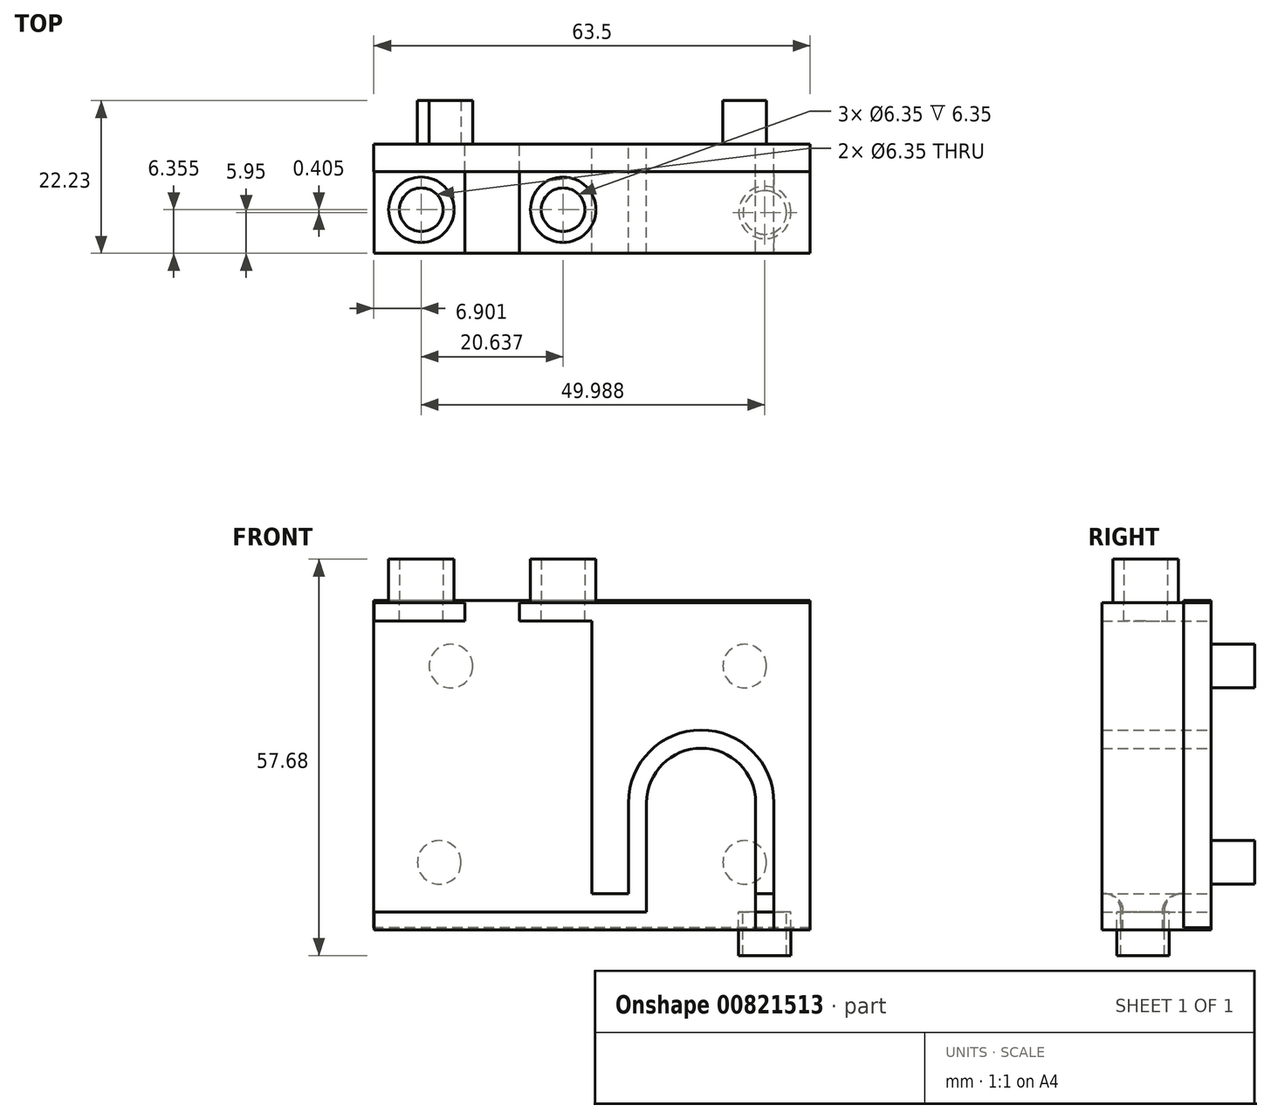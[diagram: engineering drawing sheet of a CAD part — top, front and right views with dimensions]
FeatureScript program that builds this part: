
annotation { "Feature Type Name" : "Feature", "Feature Type Description" : "" }
export const myFeature = defineFeature(function(context is Context, id is Id, definition is map)
    precondition{}
    {
        {
            var Q0;
            Q0=qCreatedBy(makeId("Front.planeOp"),FACE);
            var sketch = newSketch(context, id + "F0", { "sketchPlane" : qUnion([Q0])});
            skLineSegment(sketch, "E0.bottom", {"start": v(-31.75, 44.98) * mm, "end": v(0, 44.98) * mm});
            skLineSegment(sketch, "E0.top", {"start": v(-31.75, 0) * mm, "end": v(0, 0) * mm});
            skLineSegment(sketch, "E0.left", {"start": v(-31.75, 44.98) * mm, "end": v(-31.75, 0) * mm});
            skLineSegment(sketch, "E0.right", {"start": v(0, 44.98) * mm, "end": v(0, 0) * mm});
            skLineSegment(sketch, "E1.bottom", {"start": v(-26.46, 0) * mm, "end": v(-23.81, 0) * mm});
            skLineSegment(sketch, "E1.top", {"start": v(-26.46, 15.88) * mm, "end": v(-23.81, 15.88) * mm});
            skLineSegment(sketch, "E1.left", {"start": v(-26.46, 0) * mm, "end": v(-26.46, 15.87) * mm});
            skLineSegment(sketch, "E1.right", {"start": v(-23.81, 0) * mm, "end": v(-23.81, 15.87) * mm});
            skLineSegment(sketch, "E2.bottom", {"start": v(-7.94, 0) * mm, "end": v(-5.3, 0) * mm});
            skLineSegment(sketch, "E2.top", {"start": v(-7.94, 15.88) * mm, "end": v(-5.3, 15.88) * mm});
            skLineSegment(sketch, "E2.left", {"start": v(-7.94, 0) * mm, "end": v(-7.94, 15.87) * mm});
            skLineSegment(sketch, "E2.right", {"start": v(-5.3, 0) * mm, "end": v(-5.3, 15.87) * mm});
            skArc(sketch, "E3", {"start": v(-5.3, 15.87) * mm, "mid": v(-15.87, 26.46) * mm, "end": v(-26.46, 15.88) * mm});
            skArc(sketch, "E4", {"start": v(-7.94, 15.87) * mm, "mid": v(-15.87, 23.81) * mm, "end": v(-23.81, 15.87) * mm});
            skLineSegment(sketch, "E5.bottom", {"start": v(-26.46, 0) * mm, "end": v(-31.75, 0) * mm});
            skLineSegment(sketch, "E5.top", {"start": v(-26.46, 2.65) * mm, "end": v(-31.75, 2.65) * mm});
            skLineSegment(sketch, "E5.left", {"start": v(-26.46, 0) * mm, "end": v(-26.46, 2.65) * mm});
            skLineSegment(sketch, "E5.right", {"start": v(-31.75, 0) * mm, "end": v(-31.75, 2.65) * mm});
            skLineSegment(sketch, "E6.bottom", {"start": v(-31.75, 44.98) * mm, "end": v(-63.47, 44.98) * mm});
            skLineSegment(sketch, "E6.top", {"start": v(-31.75, 42.34) * mm, "end": v(-63.47, 42.34) * mm});
            skLineSegment(sketch, "E6.left", {"start": v(-31.75, 44.98) * mm, "end": v(-31.75, 42.34) * mm});
            skLineSegment(sketch, "E6.right", {"start": v(-63.47, 44.98) * mm, "end": v(-63.47, 42.34) * mm});
            skLineSegment(sketch, "E7.bottom", {"start": v(-63.47, 42.34) * mm, "end": v(-60.82, 42.34) * mm});
            skLineSegment(sketch, "E7.top", {"start": v(-63.47, 0) * mm, "end": v(-60.82, 0) * mm});
            skLineSegment(sketch, "E7.left", {"start": v(-63.47, 42.34) * mm, "end": v(-63.47, 0) * mm});
            skLineSegment(sketch, "E7.right", {"start": v(-60.82, 42.34) * mm, "end": v(-60.82, 0) * mm});
            skLineSegment(sketch, "E8.bottom", {"start": v(-63.47, 0) * mm, "end": v(0, 0) * mm});
            skLineSegment(sketch, "E8.top", {"start": v(-63.47, -2.65) * mm, "end": v(0, -2.65) * mm});
            skLineSegment(sketch, "E8.left", {"start": v(-63.47, 0) * mm, "end": v(-63.47, -2.65) * mm});
            skLineSegment(sketch, "E8.right", {"start": v(0, 0) * mm, "end": v(0, -2.65) * mm});
            skLineSegment(sketch, "E9.top", {"start": v(-7.94, -2.65) * mm, "end": v(-5.3, -2.65) * mm});
            skLineSegment(sketch, "E9.left", {"start": v(-7.94, 0) * mm, "end": v(-7.94, -2.65) * mm});
            skLineSegment(sketch, "E9.right", {"start": v(-5.3, 0) * mm, "end": v(-5.3, -2.65) * mm});
            skLineSegment(sketch, "E10.bottom", {"start": v(-58.18, 44.98) * mm, "end": v(-55.53, 44.98) * mm});
            skLineSegment(sketch, "E10.top", {"start": v(-58.18, 42.34) * mm, "end": v(-55.53, 42.34) * mm});
            skLineSegment(sketch, "E11.bottom", {"start": v(-50.25, 44.98) * mm, "end": v(-42.31, 44.98) * mm});
            skLineSegment(sketch, "E11.top", {"start": v(-50.25, 42.34) * mm, "end": v(-42.31, 42.34) * mm});
            skLineSegment(sketch, "E11.left", {"start": v(-50.25, 44.98) * mm, "end": v(-50.25, 42.34) * mm});
            skLineSegment(sketch, "E11.right", {"start": v(-42.31, 44.98) * mm, "end": v(-42.31, 42.34) * mm});
            skLineSegment(sketch, "E12.bottom", {"start": v(-37.04, 44.98) * mm, "end": v(-34.4, 44.98) * mm});
            skLineSegment(sketch, "E12.top", {"start": v(-37.04, 42.34) * mm, "end": v(-34.4, 42.34) * mm});
            skSolve(sketch);
        }
        {
            var Q0;
            Q0=makeQuery(id+"F0.imprint","IMPRINT",FACE,{"disambiguationData":[TD([[makeQuery(id+"F0.imprint","IMPRINT",EDGE,{"derivedFrom":sQuery(id+"F0.wireOp",EDGE,"E0.bottom")}),-1.0]])]});
            var Q1;
            {var subQ0=sQuery(id+"F0.wireOp",EDGE,"E1.right");Q1=makeQuery(id+"F0.imprint","IMPRINT",FACE,{"disambiguationData":[TD([[makeQuery(id+"F0.imprint","IMPRINT",EDGE,{"derivedFrom":subQ0}),-1.0]])]});}
            var Q2;
            {var subQ6=sQuery(id+"F0.wireOp",EDGE,"E8.left");Q2=makeQuery(id+"F0.imprint","IMPRINT",FACE,{"disambiguationData":[TD([[makeQuery(id+"F0.imprint","IMPRINT",EDGE,{"derivedFrom":subQ6}),1.0]])]});}
            var Q3;
            {var subQ0=sQuery(id+"F0.wireOp",EDGE,"E8.right");Q3=makeQuery(id+"F0.imprint","IMPRINT",FACE,{"disambiguationData":[TD([[makeQuery(id+"F0.imprint","IMPRINT",EDGE,{"derivedFrom":subQ0}),-1.0]])]});}
            var Q4;
            Q4=makeQuery(id+"F0.imprint","IMPRINT",FACE,{"disambiguationData":[TD([[makeQuery(id+"F0.imprint","IMPRINT",EDGE,{"derivedFrom":sQuery(id+"F0.wireOp",EDGE,"E7.bottom")}),-1.0]])]});
            var Q5;
            {var subQ1=sQuery(id+"F0.wireOp",EDGE,"E6.right");Q5=makeQuery(id+"F0.imprint","IMPRINT",FACE,{"disambiguationData":[TD([[makeQuery(id+"F0.imprint","IMPRINT",EDGE,{"derivedFrom":subQ1}),1.0]])]});}
            var Q6;
            {var subQ0=sQuery(id+"F0.wireOp",EDGE,"E10.right");Q6=makeQuery(id+"F0.imprint","IMPRINT",FACE,{"disambiguationData":[TD([[makeQuery(id+"F0.imprint","IMPRINT",EDGE,{"derivedFrom":subQ0}),1.0]])]});}
            var Q7;
            {var subQ0=sQuery(id+"F0.wireOp",EDGE,"E11.right");Q7=makeQuery(id+"F0.imprint","IMPRINT",FACE,{"disambiguationData":[TD([[makeQuery(id+"F0.imprint","IMPRINT",EDGE,{"derivedFrom":subQ0}),1.0]])]});}
            var Q8;
            {var subQ0=sQuery(id+"F0.wireOp",EDGE,"E6.left");Q8=makeQuery(id+"F0.imprint","IMPRINT",FACE,{"disambiguationData":[TD([[makeQuery(id+"F0.imprint","IMPRINT",EDGE,{"derivedFrom":subQ0}),-1.0]])]});}
            extrude(context, id + "F1", {"entities" : qUnion([Q0, Q1, Q2, Q3, Q4, Q5, Q6, Q7, Q8]), "depth" : 15.88 * mm, "offsetDistance" : 25.4 * mm});
        }
        {
            var Q0;
            Q0=qCreatedBy(makeId("Front.planeOp"),FACE);
            var sketch = newSketch(context, id + "F2", { "sketchPlane" : qUnion([Q0])});
            skLineSegment(sketch, "E13.bottom", {"start": v(0, 45.3) * mm, "end": v(-63.5, 45.3) * mm});
            skLineSegment(sketch, "E13.top", {"start": v(0, -2.33) * mm, "end": v(-63.5, -2.33) * mm});
            skLineSegment(sketch, "E13.left", {"start": v(0, 45.3) * mm, "end": v(0, -2.33) * mm});
            skLineSegment(sketch, "E13.right", {"start": v(-63.5, 45.3) * mm, "end": v(-63.5, -2.33) * mm});
            skCircle(sketch, "E14", {"center": v(-9.53, 35.77) * mm, "radius": 3.18 * mm});
            skCircle(sketch, "E15", {"center": v(-52.28, 35.77) * mm, "radius": 3.18 * mm});
            skCircle(sketch, "E16", {"center": v(-53.97, 7.2) * mm, "radius": 3.18 * mm});
            skCircle(sketch, "E17", {"center": v(-9.52, 7.2) * mm, "radius": 3.18 * mm});
            skSolve(sketch);
        }
        {
            var Q0;
            Q0 = qSketchRegion(id + "F2", true);
            var Q1;
            Q1=makeQuery(id+"F2.imprint","IMPRINT",FACE,{"disambiguationData":[TD([[makeQuery(id+"F2.imprint","IMPRINT",EDGE,{"derivedFrom":sQuery(id+"F2.wireOp",EDGE,"E15")}),1.0]])]});
            var Q2;
            Q2=makeQuery(id+"F2.imprint","IMPRINT",FACE,{"disambiguationData":[TD([[makeQuery(id+"F2.imprint","IMPRINT",EDGE,{"derivedFrom":sQuery(id+"F2.wireOp",EDGE,"E16")}),1.0]])]});
            var Q3;
            Q3=makeQuery(id+"F2.imprint","IMPRINT",FACE,{"disambiguationData":[TD([[makeQuery(id+"F2.imprint","IMPRINT",EDGE,{"derivedFrom":sQuery(id+"F2.wireOp",EDGE,"E17")}),1.0]])]});
            var Q4;
            Q4=makeQuery(id+"F2.imprint","IMPRINT",FACE,{"disambiguationData":[TD([[makeQuery(id+"F2.imprint","IMPRINT",EDGE,{"derivedFrom":sQuery(id+"F2.wireOp",EDGE,"E14")}),1.0]])]});
            extrude(context, id + "F3", {"entities" : qUnion([Q0, Q1, Q2, Q3, Q4]), "depth" : 3.97 * mm, "offsetDistance" : 25.4 * mm});
        }
        {
            var Q0;
            Q0=makeQuery(id+"F2.imprint","IMPRINT",FACE,{"disambiguationData":[TD([[makeQuery(id+"F2.imprint","IMPRINT",EDGE,{"derivedFrom":sQuery(id+"F2.wireOp",EDGE,"E14")}),1.0]])]});
            var Q1;
            Q1=makeQuery(id+"F2.imprint","IMPRINT",FACE,{"disambiguationData":[TD([[makeQuery(id+"F2.imprint","IMPRINT",EDGE,{"derivedFrom":sQuery(id+"F2.wireOp",EDGE,"E15")}),1.0]])]});
            var Q2;
            Q2=makeQuery(id+"F2.imprint","IMPRINT",FACE,{"disambiguationData":[TD([[makeQuery(id+"F2.imprint","IMPRINT",EDGE,{"derivedFrom":sQuery(id+"F2.wireOp",EDGE,"E17")}),1.0]])]});
            var Q3;
            Q3=makeQuery(id+"F2.imprint","IMPRINT",FACE,{"disambiguationData":[TD([[makeQuery(id+"F2.imprint","IMPRINT",EDGE,{"derivedFrom":sQuery(id+"F2.wireOp",EDGE,"E16")}),1.0]])]});
            var Q4;
            Q4=sQuery(id+"F2.wireOp",EDGE,"E14");
            var Q5;
            Q5=sQuery(id+"F2.wireOp",EDGE,"E15");
            var Q6;
            Q6=sQuery(id+"F2.wireOp",EDGE,"E17");
            var Q7;
            Q7=sQuery(id+"F2.wireOp",EDGE,"E16");
            extrude(context, id + "F4", {"entities" : qUnion([Q0, Q1, Q2, Q3]), "surfaceEntities" : qUnion([Q4, Q5, Q6, Q7]), "oppositeDirection" : true, "depth" : 6.35 * mm, "offsetDistance" : 25.4 * mm});
        }
        {
            var Q0;
            Q0=makeQuery(id+"F1.opExtrude","SWEPT_FACE",FACE,{"disambiguationData":[OSD([sQuery(id+"F0.wireOp",EDGE,"E6.bottom"),sQuery(id+"F0.wireOp",EDGE,"E10.bottom")])]});
            var sketch = newSketch(context, id + "F5", { "sketchPlane" : qUnion([Q0])});
            skCircle(sketch, "E18", {"center": v(-56.6, -9.52) * mm, "radius": 3.18 * mm});
            skCircle(sketch, "E19", {"center": v(-35.96, -9.52) * mm, "radius": 3.18 * mm});
            skCircle(sketch, "E20", {"center": v(-56.6, -9.52) * mm, "radius": 4.76 * mm});
            skCircle(sketch, "E21", {"center": v(-35.96, -9.52) * mm, "radius": 4.76 * mm});
            skSolve(sketch);
        }
        {
            var Q0;
            Q0 = qSketchRegion(id + "F5", true);
            extrude(context, id + "F6", {"entities" : qUnion([Q0]), "depth" : 6.35 * mm, "offsetDistance" : 25.4 * mm});
        }
        {
            var Q0;
            Q0=makeQuery(id+"F1.opExtrude","SWEPT_FACE",FACE,{"disambiguationData":[OSD([sQuery(id+"F0.wireOp",EDGE,"E6.bottom"),sQuery(id+"F0.wireOp",EDGE,"E10.bottom")])]});
            var sketch = newSketch(context, id + "F7", { "sketchPlane" : qUnion([Q0])});
            skCircle(sketch, "E22", {"center": v(-35.96, -9.52) * mm, "radius": 3.18 * mm});
            skCircle(sketch, "E23", {"center": v(-56.6, -9.52) * mm, "radius": 3.18 * mm});
            skSolve(sketch);
        }
        {
            var Q0;
            Q0 = qSketchRegion(id + "F7", true);
            extrude(context, id + "F8", {"entities" : qUnion([Q0]), "operationType" : NewBodyOperationType.REMOVE, "oppositeDirection" : true, "depth" : 25.4 * mm, "offsetDistance" : 25.4 * mm});
        }
        {
            var Q0;
            Q0=qCreatedBy(makeId("Top.planeOp"),FACE);
            var sketch = newSketch(context, id + "F9", { "sketchPlane" : qUnion([Q0])});
            skCircle(sketch, "E24", {"center": v(-6.61, -9.93) * mm, "radius": 3.81 * mm});
            skCircle(sketch, "E25", {"center": v(-6.61, -9.93) * mm, "radius": 3.18 * mm});
            skSolve(sketch);
        }
        {
            var Q0;
            Q0 = qSketchRegion(id + "F9", true);
            extrude(context, id + "F10", {"entities" : qUnion([Q0]), "oppositeDirection" : true, "depth" : 6.35 * mm, "offsetDistance" : 25.4 * mm});
        }
        {
            var Q0;
            Q0=qCreatedBy(makeId("Top.planeOp"),FACE);
            var sketch = newSketch(context, id + "F11", { "sketchPlane" : qUnion([Q0])});
            skLineSegment(sketch, "E26.bottom", {"start": v(-7.96, -15.88) * mm, "end": v(-5.31, -15.88) * mm});
            skLineSegment(sketch, "E26.top", {"start": v(-7.96, -3.95) * mm, "end": v(-5.31, -3.95) * mm});
            skLineSegment(sketch, "E26.left", {"start": v(-7.96, -15.88) * mm, "end": v(-7.96, -3.95) * mm});
            skLineSegment(sketch, "E26.right", {"start": v(-5.31, -15.88) * mm, "end": v(-5.31, -3.95) * mm});
            skCircle(sketch, "E27", {"center": v(-6.61, -9.93) * mm, "radius": 3.17 * mm});
            skSolve(sketch);
        }
        {
            var Q0;
            Q0=makeQuery(id+"F11.imprint","IMPRINT",FACE,{"disambiguationData":[TD([[makeQuery(id+"F11.imprint","IMPRINT",EDGE,{"derivedFrom":sQuery(id+"F11.wireOp",EDGE,"E26.bottom")}),1.0]])]});
            var Q1;
            {var subQ0=sQuery(id+"F11.wireOp",EDGE,"E26.top");Q1=makeQuery(id+"F11.imprint","IMPRINT",FACE,{"disambiguationData":[TD([[makeQuery(id+"F11.imprint","IMPRINT",EDGE,{"derivedFrom":subQ0}),-1.0]])]});}
            extrude(context, id + "F12", {"entities" : qUnion([Q0, Q1]), "depth" : 2.65 * mm, "offsetDistance" : 25.4 * mm});
        }
        {
            var Q0;
            Q0=makeQuery(id+"F12.opExtrude","CAP_FACE",FACE,{"disambiguationData":[OSD([sQuery(id+"F11.wireOp",EDGE,"E26.bottom"),sQuery(id+"F11.wireOp",EDGE,"E26.left"),sQuery(id+"F11.wireOp",EDGE,"E26.right"),sQuery(id+"F11.wireOp",EDGE,"E27")])],"isStart":true});
            var Q1;
            Q1=makeQuery(id+"F12.opExtrude","CAP_FACE",FACE,{"disambiguationData":[OSD([sQuery(id+"F11.wireOp",EDGE,"E26.top"),sQuery(id+"F11.wireOp",EDGE,"E26.left"),sQuery(id+"F11.wireOp",EDGE,"E26.right"),sQuery(id+"F11.wireOp",EDGE,"E27")])],"isStart":true});
            extrude(context, id + "F13", {"entities" : qUnion([Q0, Q1]), "depth" : 2.65 * mm, "offsetDistance" : 25.4 * mm});
        }
        {
            var Q0;
            {var subQ0=sQuery(id+"F11.wireOp",EDGE,"E27");Q0=makeQuery(id+"F12.opExtrude","CAP_EDGE",EDGE,{"disambiguationData":[OSD([subQ0]),TDD([makeQuery(id+"F11.imprint","IMPRINT",EDGE,{"disambiguationData":[TD([[makeQuery(id+"F11.imprint","INTERSECT",VERTEX,{"disambiguationData":[OD(1.0)],"derivedFrom":[sQuery(id+"F11.wireOp",EDGE,"E26.left"),subQ0]}),1.0]])],"derivedFrom":subQ0})])],"isStart":false});}
            var Q1;
            {var subQ0=sQuery(id+"F11.wireOp",EDGE,"E27");Q1=makeQuery(id+"F12.opExtrude","CAP_EDGE",EDGE,{"disambiguationData":[OSD([subQ0]),TDD([makeQuery(id+"F11.imprint","IMPRINT",EDGE,{"disambiguationData":[TD([[makeQuery(id+"F11.imprint","INTERSECT",VERTEX,{"disambiguationData":[OD(0.0)],"derivedFrom":[sQuery(id+"F11.wireOp",EDGE,"E26.left"),subQ0]}),-1.0]])],"derivedFrom":subQ0})])],"isStart":false});}
            fillet(context, id + "F14", {"entities" : qUnion([Q0, Q1]), "radius" : 2.54 * mm, "tangentPropagation" : true, "allowEdgeOverflow" : false});
        }
    });
